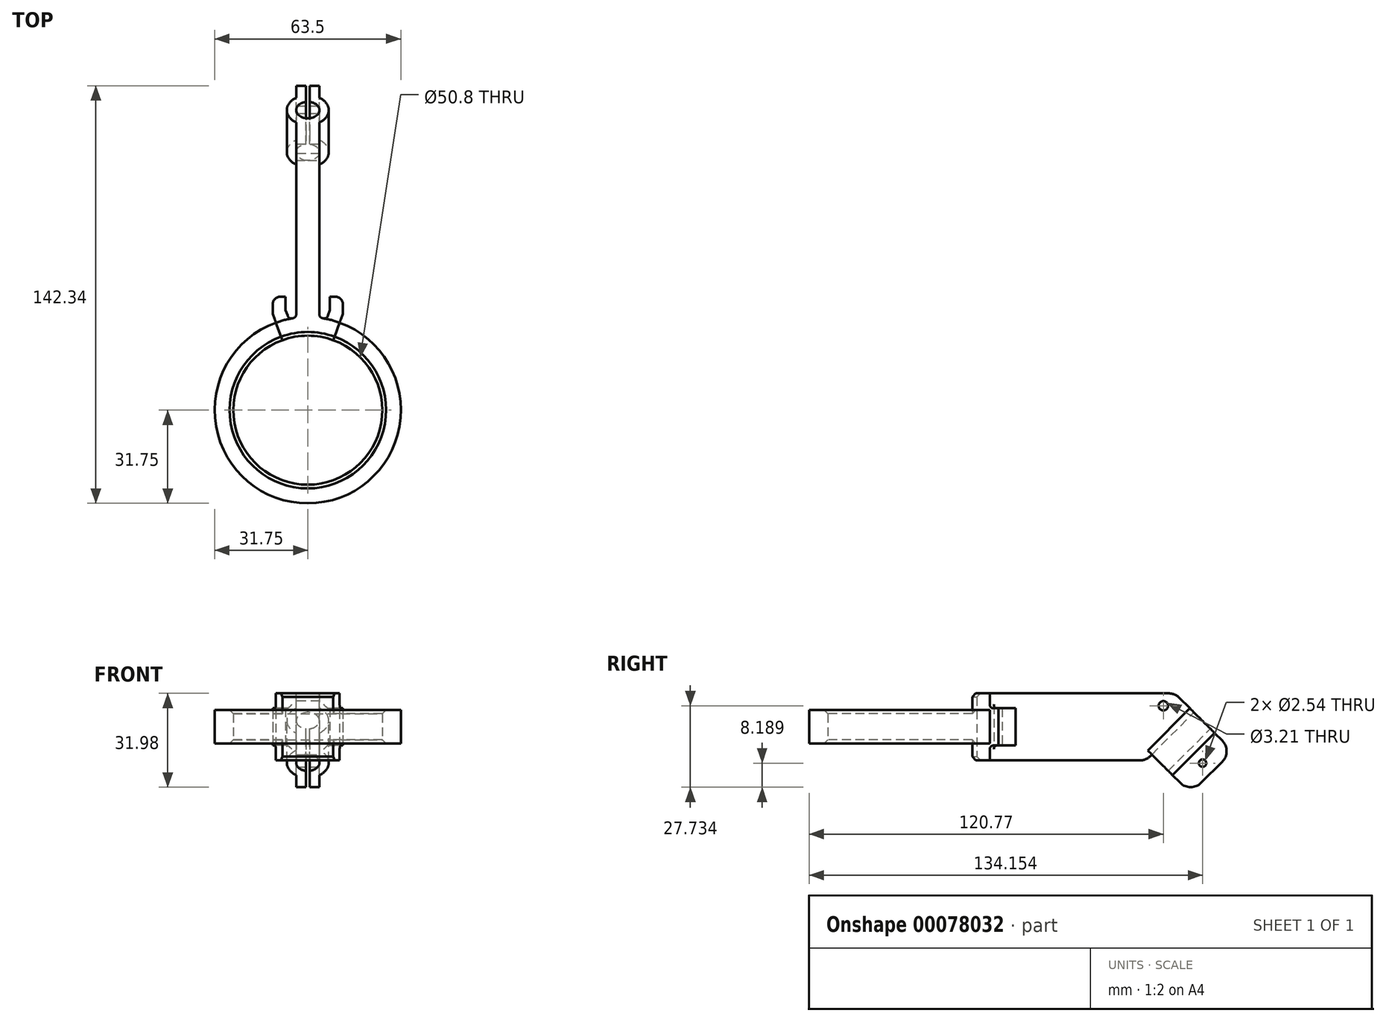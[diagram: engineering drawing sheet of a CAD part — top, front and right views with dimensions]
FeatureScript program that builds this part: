
annotation { "Feature Type Name" : "Feature", "Feature Type Description" : "" }
export const myFeature = defineFeature(function(context is Context, id is Id, definition is map)
    precondition{}
    {
        {
            var Q0;
            Q0=qCreatedBy(makeId("Right.planeOp"),FACE);
            var sketch = newSketch(context, id + "F0", { "sketchPlane" : qUnion([Q0])});
            skLineSegment(sketch, "E0.bottom", {"start": v(-25.4, 11.43) * mm, "end": v(25.4, 11.43) * mm});
            skLineSegment(sketch, "E0.top", {"start": v(-25.4, -11.43) * mm, "end": v(25.4, -11.43) * mm});
            skLineSegment(sketch, "E0.left", {"start": v(-25.4, 11.43) * mm, "end": v(-25.4, -11.43) * mm});
            skLineSegment(sketch, "E0.right", {"start": v(25.4, 11.43) * mm, "end": v(25.4, -11.43) * mm});
            skLineSegment(sketch, "E1", {"start": v(25.4, 11.43) * mm, "end": v(-25.4, -11.43) * mm, "construction": true});
            skLineSegment(sketch, "E2", {"start": v(-25.4, 11.43) * mm, "end": v(25.4, -11.43) * mm, "construction": true});
            skLineSegment(sketch, "E3.bottom", {"start": v(25.4, 11.43) * mm, "end": v(101.47, 11.43) * mm});
            skLineSegment(sketch, "E3.top", {"start": v(25.4, -11.43) * mm, "end": v(101.47, -11.43) * mm});
            skLineSegment(sketch, "E3.right", {"start": v(101.47, 11.43) * mm, "end": v(101.47, -11.43) * mm});
            skLineSegment(sketch, "E4", {"start": v(101.47, 11.43) * mm, "end": v(78.61, -11.43) * mm});
            skLineSegment(sketch, "E5", {"start": v(101.47, 11.43) * mm, "end": v(122.24, -9.34) * mm});
            skLineSegment(sketch, "E6", {"start": v(122.24, -9.34) * mm, "end": v(99.38, -32.2) * mm});
            skLineSegment(sketch, "E7", {"start": v(99.38, -32.2) * mm, "end": v(78.61, -11.43) * mm});
            skLineSegment(sketch, "E8", {"start": v(31.75, 11.43) * mm, "end": v(31.75, -11.43) * mm});
            skLineSegment(sketch, "E9", {"start": v(34.92, 11.43) * mm, "end": v(34.92, -11.43) * mm});
            skLineSegment(sketch, "E10", {"start": v(37.46, 11.43) * mm, "end": v(37.47, -11.43) * mm});
            skSolve(sketch);
        }
        {
            var Q0;
            Q0=sQuery(id+"F0.wireOp",EDGE,"E4");
            cPlane(context, id + "F1", {"entities" : qUnion([Q0]), "cplaneType" : CPlaneType.MID_PLANE, "offset" : 152.4 * mm, "width" : 152.4 * mm, "height" : 152.4 * mm});
        }
        {
            var Q0;
            Q0=qCreatedBy(id+"F1.planeOp",FACE);
            var sketch = newSketch(context, id + "F2", { "sketchPlane" : qUnion([Q0])});
            skLineSegment(sketch, "E11.0", {"start": v(0, -63.67) * mm, "end": v(0, -93.04) * mm, "construction": true});
            skArc(sketch, "E12", {"start": v(0.64, -74.73) * mm, "mid": v(0, -66.85) * mm, "end": v(-0.64, -74.73) * mm});
            skArc(sketch, "E13", {"start": v(3.97, -76.75) * mm, "mid": v(0, -63.67) * mm, "end": v(-3.97, -76.75) * mm});
            skLineSegment(sketch, "E14", {"start": v(-3.97, -70.81) * mm, "end": v(-3.97, -85.55) * mm, "construction": true});
            skLineSegment(sketch, "E15", {"start": v(-3.97, -85.55) * mm, "end": v(-0.64, -85.55) * mm});
            skLineSegment(sketch, "E16", {"start": v(-0.64, -85.55) * mm, "end": v(-0.64, -77.93) * mm});
            skLineSegment(sketch, "E17", {"start": v(-3.97, -85.55) * mm, "end": v(-3.97, -76.75) * mm});
            skLineSegment(sketch, "E18.MirrorCS", {"start": v(0.64, -85.55) * mm, "end": v(0.64, -77.93) * mm});
            skLineSegment(sketch, "E19.MirrorCS", {"start": v(3.97, -85.55) * mm, "end": v(0.64, -85.55) * mm});
            skLineSegment(sketch, "E20.MirrorCS", {"start": v(3.97, -85.55) * mm, "end": v(3.97, -76.75) * mm});
            skLineSegment(sketch, "E21", {"start": v(-0.64, -77.93) * mm, "end": v(-0.64, -74.73) * mm});
            skLineSegment(sketch, "E22", {"start": v(0.64, -77.93) * mm, "end": v(0.64, -74.73) * mm});
            skSolve(sketch);
        }
        {
            var Q0;
            Q0 = qSketchRegion(id + "F2", true);
            extrude(context, id + "F3", {"entities" : qUnion([Q0]), "endBound" : BoundingType.SYMMETRIC, "depth" : 20.32 * mm});
        }
        {
            var Q0;
            Q0=qCreatedBy(makeId("Right.planeOp"),FACE);
            var sketch = newSketch(context, id + "F4", { "sketchPlane" : qUnion([Q0])});
            skLineSegment(sketch, "E23.0", {"start": v(25.4, 11.43) * mm, "end": v(25.4, -11.43) * mm});
            skLineSegment(sketch, "E23.1", {"start": v(25.4, 11.43) * mm, "end": v(92.98, 11.43) * mm});
            skLineSegment(sketch, "E23.2", {"start": v(25.4, -11.43) * mm, "end": v(78.61, -11.43) * mm});
            skLineSegment(sketch, "E24.0", {"start": v(101.47, 11.43) * mm, "end": v(78.61, -11.43) * mm, "construction": true});
            skPoint(sketch, "E25.orphan", {"position": v(101.47, -11.43) * mm});
            skLineSegment(sketch, "E26.0", {"start": v(99.38, -32.2) * mm, "end": v(78.61, -11.43) * mm, "construction": true});
            skLineSegment(sketch, "E26.1", {"start": v(101.47, 11.43) * mm, "end": v(122.24, -9.34) * mm, "construction": true});
            skLineSegment(sketch, "E27", {"start": v(83.1, -11.43) * mm, "end": v(99.47, 4.94) * mm, "construction": true});
            skLineSegment(sketch, "E28.0", {"start": v(106.48, -2.07) * mm, "end": v(97.23, 7.18) * mm, "construction": true});
            skLineSegment(sketch, "E29", {"start": v(99.47, 4.94) * mm, "end": v(92.98, 11.43) * mm});
            skLineSegment(sketch, "E30", {"start": v(99.47, 4.94) * mm, "end": v(83.1, -11.43) * mm});
            skPoint(sketch, "E31.orphan", {"position": v(101.47, 11.43) * mm});
            skLineSegment(sketch, "E32", {"start": v(78.61, -11.43) * mm, "end": v(83.1, -11.43) * mm});
            skCircle(sketch, "E33", {"center": v(89.02, 7.18) * mm, "radius": 1.6 * mm});
            skSolve(sketch);
        }
        {
            var Q0;
            Q0 = qSketchRegion(id + "F4", true);
            extrude(context, id + "F5", {"entities" : qUnion([Q0]), "operationType" : NewBodyOperationType.ADD, "endBound" : BoundingType.SYMMETRIC, "depth" : 7.94 * mm});
        }
        {
            var Q0;
            Q0=qCreatedBy(makeId("Top.planeOp"),FACE);
            var sketch = newSketch(context, id + "F6", { "sketchPlane" : qUnion([Q0])});
            skArc(sketch, "E34", {"start": v(8.69, 23.87) * mm, "mid": v(0, 25.4) * mm, "end": v(-8.69, 23.87) * mm});
            skArc(sketch, "E35", {"start": v(6.45, 31.09) * mm, "mid": v(0, 31.75) * mm, "end": v(-6.45, 31.09) * mm});
            skArc(sketch, "E36", {"start": v(-7.55, 34.1) * mm, "mid": v(-9.77, 33.53) * mm, "end": v(-11.95, 32.82) * mm, "construction": true});
            skLineSegment(sketch, "E37", {"start": v(8.69, 23.87) * mm, "end": v(11.95, 32.82) * mm});
            skLineSegment(sketch, "E38", {"start": v(0, 0) * mm, "end": v(0, 61.85) * mm, "construction": true});
            skLineSegment(sketch, "E39", {"start": v(6.45, 31.09) * mm, "end": v(7.55, 34.1) * mm});
            skLineSegment(sketch, "E40.0", {"start": v(3.97, 31.5) * mm, "end": v(3.97, 92.98) * mm});
            skLineSegment(sketch, "E41", {"start": v(7.55, 34.1) * mm, "end": v(7.55, 38.67) * mm});
            skLineSegment(sketch, "E42", {"start": v(7.55, 38.67) * mm, "end": v(11.95, 38.67) * mm});
            skLineSegment(sketch, "E43", {"start": v(11.95, 38.67) * mm, "end": v(11.95, 32.82) * mm});
            skPoint(sketch, "E44.orphan", {"position": v(3.97, 25.4) * mm});
            skLineSegment(sketch, "E45.MirrorCS", {"start": v(-8.69, 23.87) * mm, "end": v(-11.95, 32.82) * mm});
            skLineSegment(sketch, "E46.MirrorCS", {"start": v(-6.45, 31.09) * mm, "end": v(-7.55, 34.1) * mm});
            skLineSegment(sketch, "E47.MirrorCS", {"start": v(-7.55, 34.1) * mm, "end": v(-7.55, 38.67) * mm});
            skLineSegment(sketch, "E48.MirrorCS", {"start": v(-7.55, 38.67) * mm, "end": v(-11.95, 38.67) * mm});
            skLineSegment(sketch, "E49.MirrorCS", {"start": v(-11.95, 38.67) * mm, "end": v(-11.95, 32.82) * mm});
            skPoint(sketch, "E50.orphan", {"position": v(-3.97, 92.98) * mm});
            skPoint(sketch, "E40.1.start.orphan", {"position": v(-3.97, 25.4) * mm});
            skArc(sketch, "E51.trimOffspring", {"start": v(11.95, 32.82) * mm, "mid": v(9.77, 33.53) * mm, "end": v(7.55, 34.1) * mm, "construction": true});
            skSolve(sketch);
        }
        {
            var Q0;
            Q0 = qSketchRegion(id + "F6", true);
            extrude(context, id + "F7", {"entities" : qUnion([Q0]), "operationType" : NewBodyOperationType.ADD, "endBound" : BoundingType.SYMMETRIC, "depth" : 12.7 * mm});
        }
        {
            var Q0;
            Q0=qCreatedBy(makeId("Top.planeOp"),FACE);
            var sketch = newSketch(context, id + "F8", { "sketchPlane" : qUnion([Q0])});
            skArc(sketch, "E52", {"start": v(8.69, 23.87) * mm, "mid": v(0, 25.4) * mm, "end": v(-8.69, 23.87) * mm});
            skArc(sketch, "E53", {"start": v(10.86, 29.84) * mm, "mid": v(0, 31.75) * mm, "end": v(-10.86, 29.84) * mm});
            skLineSegment(sketch, "E54.0", {"start": v(8.69, 23.87) * mm, "end": v(10.86, 29.84) * mm});
            skPoint(sketch, "E55.orphan", {"position": v(11.95, 32.82) * mm});
            skLineSegment(sketch, "E56.MirrorCS", {"start": v(-8.69, 23.87) * mm, "end": v(-10.86, 29.84) * mm});
            skSolve(sketch);
        }
        {
            var Q0;
            Q0 = qSketchRegion(id + "F8", true);
            extrude(context, id + "F9", {"entities" : qUnion([Q0]), "operationType" : NewBodyOperationType.ADD, "endBound" : BoundingType.SYMMETRIC, "depth" : 22.86 * mm});
        }
        {
            var Q0;
            Q0=makeQuery(id+"F7.opExtrude","SWEPT_EDGE",EDGE,{"disambiguationData":[OSD([sQuery(id+"F6.wireOp",EDGE,"E35"),sQuery(id+"F6.wireOp",EDGE,"E46.MirrorCS")])]});
            var Q1;
            Q1=makeQuery(id+"F9.boolean.opBoolean","INTERSECT",EDGE,{"derivedFrom":[makeQuery(id+"F5.opExtrude","CAP_FACE",FACE,{"disambiguationData":[OSD([sQuery(id+"F4.wireOp",EDGE,"E23.0"),sQuery(id+"F4.wireOp",EDGE,"E23.1"),sQuery(id+"F4.wireOp",EDGE,"E23.2"),sQuery(id+"F4.wireOp",EDGE,"E29"),sQuery(id+"F4.wireOp",EDGE,"E30"),sQuery(id+"F4.wireOp",EDGE,"E32")])],"isStart":true}),makeQuery(id+"F9.opExtrude","SWEPT_FACE",FACE,{"disambiguationData":[OSD([sQuery(id+"F8.wireOp",EDGE,"E53")])]})]});
            var Q2;
            Q2=makeQuery(id+"F9.boolean.opBoolean","INTERSECT",EDGE,{"derivedFrom":[makeQuery(id+"F5.opExtrude","CAP_FACE",FACE,{"disambiguationData":[OSD([sQuery(id+"F4.wireOp",EDGE,"E23.0"),sQuery(id+"F4.wireOp",EDGE,"E23.1"),sQuery(id+"F4.wireOp",EDGE,"E23.2"),sQuery(id+"F4.wireOp",EDGE,"E29"),sQuery(id+"F4.wireOp",EDGE,"E30"),sQuery(id+"F4.wireOp",EDGE,"E32")])],"isStart":false}),makeQuery(id+"F9.opExtrude","SWEPT_FACE",FACE,{"disambiguationData":[OSD([sQuery(id+"F8.wireOp",EDGE,"E53")])]})]});
            var Q3;
            Q3=makeQuery(id+"F7.opExtrude","SWEPT_EDGE",EDGE,{"disambiguationData":[OSD([sQuery(id+"F6.wireOp",EDGE,"E35"),sQuery(id+"F6.wireOp",EDGE,"E39")])]});
            fillet(context, id + "F10", {"entities" : qUnion([Q0, Q1, Q2, Q3]), "radius" : 1.27 * mm, "tangentPropagation" : true, "allowEdgeOverflow" : false});
        }
        {
            var Q0;
            {var subQ0=sQuery(id+"F6.wireOp",EDGE,"E49.MirrorCS");var subQ1=sQuery(id+"F6.wireOp",EDGE,"E48.MirrorCS");var subQ2=sQuery(id+"F6.wireOp",EDGE,"E47.MirrorCS");var subQ3=sQuery(id+"F6.wireOp",EDGE,"E46.MirrorCS");var subQ4=sQuery(id+"F6.wireOp",EDGE,"E45.MirrorCS");var subQ5=sQuery(id+"F6.wireOp",EDGE,"E35");var subQ6=sQuery(id+"F6.wireOp",EDGE,"E34");var subQ7=makeQuery(id+"F7.opExtrude","CAP_FACE",FACE,{"disambiguationData":[OSD([subQ6,subQ5,sQuery(id+"F6.wireOp",EDGE,"E37"),sQuery(id+"F6.wireOp",EDGE,"E39"),sQuery(id+"F6.wireOp",EDGE,"E41"),sQuery(id+"F6.wireOp",EDGE,"E42"),sQuery(id+"F6.wireOp",EDGE,"E43"),subQ4,subQ3,subQ2,subQ1,subQ0])],"isStart":false});Q0=makeQuery(id+"F9.boolean.opBoolean","INTERSECT",EDGE,{"derivedFrom":[makeQuery(id+"F7.boolean.opBoolean","SPLIT",FACE,{"disambiguationData":[TD([makeQuery(id+"F7.opExtrude","SWEPT_FACE",FACE,{"disambiguationData":[OSD([subQ4])]})])],"derivedFrom":subQ7}),makeQuery(id+"F9.opExtrude","SWEPT_FACE",FACE,{"disambiguationData":[OSD([sQuery(id+"F8.wireOp",EDGE,"E53")])]})]});}
            var Q1;
            {var subQ0=sQuery(id+"F6.wireOp",EDGE,"E43");var subQ1=sQuery(id+"F6.wireOp",EDGE,"E42");var subQ2=sQuery(id+"F6.wireOp",EDGE,"E41");var subQ3=sQuery(id+"F6.wireOp",EDGE,"E39");var subQ4=sQuery(id+"F6.wireOp",EDGE,"E37");var subQ5=sQuery(id+"F6.wireOp",EDGE,"E35");var subQ6=sQuery(id+"F6.wireOp",EDGE,"E34");var subQ7=makeQuery(id+"F7.opExtrude","CAP_FACE",FACE,{"disambiguationData":[OSD([subQ6,subQ5,subQ4,subQ3,subQ2,subQ1,subQ0,sQuery(id+"F6.wireOp",EDGE,"E45.MirrorCS"),sQuery(id+"F6.wireOp",EDGE,"E46.MirrorCS"),sQuery(id+"F6.wireOp",EDGE,"E47.MirrorCS"),sQuery(id+"F6.wireOp",EDGE,"E48.MirrorCS"),sQuery(id+"F6.wireOp",EDGE,"E49.MirrorCS")])],"isStart":false});Q1=makeQuery(id+"F9.boolean.opBoolean","INTERSECT",EDGE,{"derivedFrom":[makeQuery(id+"F7.boolean.opBoolean","SPLIT",FACE,{"disambiguationData":[TD([makeQuery(id+"F7.opExtrude","SWEPT_FACE",FACE,{"disambiguationData":[OSD([subQ4])]})])],"derivedFrom":subQ7}),makeQuery(id+"F9.opExtrude","SWEPT_FACE",FACE,{"disambiguationData":[OSD([sQuery(id+"F8.wireOp",EDGE,"E53")])]})]});}
            var Q2;
            {var subQ0=sQuery(id+"F6.wireOp",EDGE,"E43");var subQ1=sQuery(id+"F6.wireOp",EDGE,"E42");var subQ2=sQuery(id+"F6.wireOp",EDGE,"E41");var subQ3=sQuery(id+"F6.wireOp",EDGE,"E39");var subQ4=sQuery(id+"F6.wireOp",EDGE,"E37");var subQ5=sQuery(id+"F6.wireOp",EDGE,"E35");var subQ6=sQuery(id+"F6.wireOp",EDGE,"E34");var subQ7=makeQuery(id+"F7.opExtrude","CAP_FACE",FACE,{"disambiguationData":[OSD([subQ6,subQ5,subQ4,subQ3,subQ2,subQ1,subQ0,sQuery(id+"F6.wireOp",EDGE,"E45.MirrorCS"),sQuery(id+"F6.wireOp",EDGE,"E46.MirrorCS"),sQuery(id+"F6.wireOp",EDGE,"E47.MirrorCS"),sQuery(id+"F6.wireOp",EDGE,"E48.MirrorCS"),sQuery(id+"F6.wireOp",EDGE,"E49.MirrorCS")])],"isStart":true});Q2=makeQuery(id+"F9.boolean.opBoolean","INTERSECT",EDGE,{"derivedFrom":[makeQuery(id+"F7.boolean.opBoolean","SPLIT",FACE,{"disambiguationData":[TD([makeQuery(id+"F7.opExtrude","SWEPT_FACE",FACE,{"disambiguationData":[OSD([subQ4])]})])],"derivedFrom":subQ7}),makeQuery(id+"F9.opExtrude","SWEPT_FACE",FACE,{"disambiguationData":[OSD([sQuery(id+"F8.wireOp",EDGE,"E53")])]})]});}
            var Q3;
            {var subQ0=sQuery(id+"F6.wireOp",EDGE,"E49.MirrorCS");var subQ1=sQuery(id+"F6.wireOp",EDGE,"E48.MirrorCS");var subQ2=sQuery(id+"F6.wireOp",EDGE,"E47.MirrorCS");var subQ3=sQuery(id+"F6.wireOp",EDGE,"E46.MirrorCS");var subQ4=sQuery(id+"F6.wireOp",EDGE,"E45.MirrorCS");var subQ5=sQuery(id+"F6.wireOp",EDGE,"E35");var subQ6=sQuery(id+"F6.wireOp",EDGE,"E34");var subQ7=makeQuery(id+"F7.opExtrude","CAP_FACE",FACE,{"disambiguationData":[OSD([subQ6,subQ5,sQuery(id+"F6.wireOp",EDGE,"E37"),sQuery(id+"F6.wireOp",EDGE,"E39"),sQuery(id+"F6.wireOp",EDGE,"E41"),sQuery(id+"F6.wireOp",EDGE,"E42"),sQuery(id+"F6.wireOp",EDGE,"E43"),subQ4,subQ3,subQ2,subQ1,subQ0])],"isStart":true});Q3=makeQuery(id+"F9.boolean.opBoolean","INTERSECT",EDGE,{"derivedFrom":[makeQuery(id+"F7.boolean.opBoolean","SPLIT",FACE,{"disambiguationData":[TD([makeQuery(id+"F7.opExtrude","SWEPT_FACE",FACE,{"disambiguationData":[OSD([subQ4])]})])],"derivedFrom":subQ7}),makeQuery(id+"F9.opExtrude","SWEPT_FACE",FACE,{"disambiguationData":[OSD([sQuery(id+"F8.wireOp",EDGE,"E53")])]})]});}
            fillet(context, id + "F11", {"entities" : qUnion([Q0, Q1, Q2, Q3]), "radius" : 1.27 * mm, "tangentPropagation" : true, "allowEdgeOverflow" : false});
        }
        {
            var Q0;
            Q0=makeQuery(id+"F5.opExtrude","SWEPT_EDGE",EDGE,{"disambiguationData":[OSD([sQuery(id+"F4.wireOp",EDGE,"E23.1"),sQuery(id+"F4.wireOp",EDGE,"E29")])]});
            fillet(context, id + "F12", {"entities" : qUnion([Q0]), "radius" : 5.08 * mm, "tangentPropagation" : true, "allowEdgeOverflow" : false});
        }
        {
            var Q0;
            Q0=makeQuery(id+"F5.opExtrude","SWEPT_EDGE",EDGE,{"disambiguationData":[OSD([sQuery(id+"F4.wireOp",EDGE,"E30"),sQuery(id+"F4.wireOp",EDGE,"E32")])]});
            fillet(context, id + "F13", {"entities" : qUnion([Q0]), "radius" : 5.08 * mm, "tangentPropagation" : true, "allowEdgeOverflow" : false});
        }
        {
            var Q0;
            Q0=makeQuery(id+"F3.opExtrude","CAP_EDGE",EDGE,{"disambiguationData":[OSD([sQuery(id+"F2.wireOp",EDGE,"E19.MirrorCS")])],"isStart":true});
            var Q1;
            Q1=makeQuery(id+"F3.opExtrude","CAP_EDGE",EDGE,{"disambiguationData":[OSD([sQuery(id+"F2.wireOp",EDGE,"E15")])],"isStart":true});
            var Q2;
            Q2=makeQuery(id+"F3.opExtrude","CAP_EDGE",EDGE,{"disambiguationData":[OSD([sQuery(id+"F2.wireOp",EDGE,"E15")])],"isStart":false});
            var Q3;
            Q3=makeQuery(id+"F3.opExtrude","CAP_EDGE",EDGE,{"disambiguationData":[OSD([sQuery(id+"F2.wireOp",EDGE,"E19.MirrorCS")])],"isStart":false});
            fillet(context, id + "F14", {"entities" : qUnion([Q0, Q1, Q2, Q3]), "radius" : 5.08 * mm, "tangentPropagation" : true, "allowEdgeOverflow" : false});
        }
        {
            var Q0;
            Q0=makeQuery(id+"F7.opExtrude","SWEPT_EDGE",EDGE,{"disambiguationData":[OSD([sQuery(id+"F6.wireOp",EDGE,"E42"),sQuery(id+"F6.wireOp",EDGE,"E43")])]});
            var Q1;
            Q1=makeQuery(id+"F7.opExtrude","SWEPT_EDGE",EDGE,{"disambiguationData":[OSD([sQuery(id+"F6.wireOp",EDGE,"E48.MirrorCS"),sQuery(id+"F6.wireOp",EDGE,"E49.MirrorCS")])]});
            fillet(context, id + "F15", {"entities" : qUnion([Q0, Q1]), "radius" : 2.54 * mm, "tangentPropagation" : true, "allowEdgeOverflow" : false});
        }
        {
            var Q0;
            Q0=makeQuery(id+"F3.opExtrude","SWEPT_FACE",FACE,{"disambiguationData":[OSD([sQuery(id+"F2.wireOp",EDGE,"E20.MirrorCS")])]});
            var sketch = newSketch(context, id + "F16", { "sketchPlane" : qUnion([Q0])});
            skLineSegment(sketch, "E57.0", {"start": v(101.92, -19.06) * mm, "end": v(109.1, -11.88) * mm, "construction": true});
            skLineSegment(sketch, "E57.1", {"start": v(92.11, -16.44) * mm, "end": v(106.48, -2.07) * mm, "construction": true});
            skLineSegment(sketch, "E58", {"start": v(99.3, -9.25) * mm, "end": v(105.51, -15.47) * mm, "construction": true});
            skCircle(sketch, "E59", {"center": v(102.4, -12.36) * mm, "radius": 1.27 * mm});
            skSolve(sketch);
        }
        {
            var Q0;
            Q0 = qSketchRegion(id + "F16", true);
            extrude(context, id + "F17", {"entities" : qUnion([Q0]), "operationType" : NewBodyOperationType.REMOVE, "endBound" : BoundingType.THROUGH_ALL, "oppositeDirection" : true, "depth" : 25.4 * mm});
        }
        {
            var Q0;
            Q0=qCreatedBy(makeId("Top.planeOp"),FACE);
            var sketch = newSketch(context, id + "F18", { "sketchPlane" : qUnion([Q0])});
            skCircle(sketch, "E60", {"center": v(0, 0) * mm, "radius": 25.4 * mm});
            skCircle(sketch, "E61", {"center": v(0, 0) * mm, "radius": 31.75 * mm});
            skSolve(sketch);
        }
        {
            var Q0;
            Q0 = qSketchRegion(id + "F18", true);
            extrude(context, id + "F19", {"entities" : qUnion([Q0]), "operationType" : NewBodyOperationType.ADD, "endBound" : BoundingType.SYMMETRIC, "depth" : 11.43 * mm});
        }
        {
            var Q0;
            Q0=makeQuery(id+"F19.opExtrude","CAP_EDGE",EDGE,{"disambiguationData":[OSD([sQuery(id+"F18.wireOp",EDGE,"E60")])],"isStart":false});
            var Q1;
            Q1=makeQuery(id+"F19.opExtrude","CAP_EDGE",EDGE,{"disambiguationData":[OSD([sQuery(id+"F18.wireOp",EDGE,"E60")])],"isStart":true});
            var Q2;
            Q2=makeQuery(id+"F9.opExtrude","CAP_EDGE",EDGE,{"disambiguationData":[OSD([sQuery(id+"F8.wireOp",EDGE,"E52")])],"isStart":true});
            var Q3;
            Q3=makeQuery(id+"F9.opExtrude","CAP_EDGE",EDGE,{"disambiguationData":[OSD([sQuery(id+"F8.wireOp",EDGE,"E52")])],"isStart":false});
            chamfer(context, id + "F20", {"entities" : qUnion([Q0, Q1, Q2, Q3]), "width" : 1.27 * mm, "tangentPropagation" : true});
        }
    });
